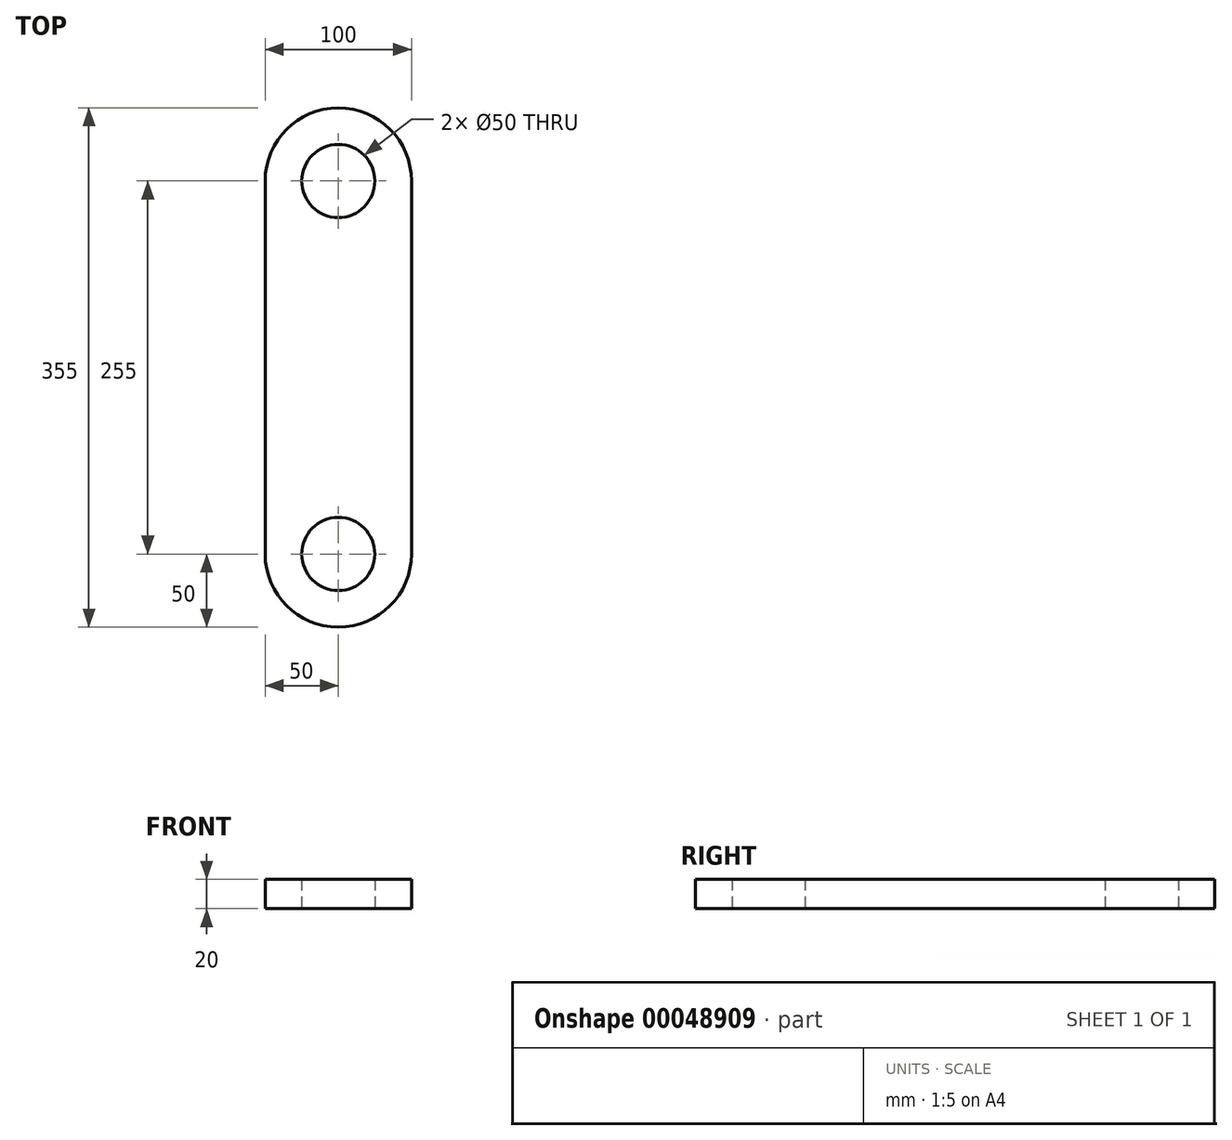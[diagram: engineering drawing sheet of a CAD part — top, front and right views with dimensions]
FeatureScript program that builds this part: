
annotation { "Feature Type Name" : "Feature", "Feature Type Description" : "" }
export const myFeature = defineFeature(function(context is Context, id is Id, definition is map)
    precondition{}
    {
        {
            var Q0;
            Q0=qCreatedBy(makeId("Top.planeOp"),FACE);
            var sketch = newSketch(context, id + "F0", { "sketchPlane" : qUnion([Q0])});
            skCircle(sketch, "E0", {"center": v(0, 0) * mm, "radius": 25 * mm});
            skCircle(sketch, "E1", {"center": v(0, 0) * mm, "radius": 50 * mm});
            skLineSegment(sketch, "E2", {"start": v(0, 0) * mm, "end": v(0, -255) * mm, "construction": true});
            skCircle(sketch, "E3", {"center": v(0, -255) * mm, "radius": 25 * mm});
            skCircle(sketch, "E4", {"center": v(0, -255) * mm, "radius": 50 * mm});
            skLineSegment(sketch, "E5", {"start": v(-50, 0) * mm, "end": v(50, 0) * mm, "construction": true});
            skLineSegment(sketch, "E6", {"start": v(-50, -255) * mm, "end": v(50, -255) * mm, "construction": true});
            skLineSegment(sketch, "E7", {"start": v(-50, 0) * mm, "end": v(-50, -255) * mm});
            skLineSegment(sketch, "E8", {"start": v(50, 0) * mm, "end": v(50, -255) * mm});
            skSolve(sketch);
        }
        {
            var Q0;
            Q0 = qSketchRegion(id + "F0", true);
            extrude(context, id + "F1", {"entities" : qUnion([Q0]), "depth" : 20 * mm});
        }
    });
